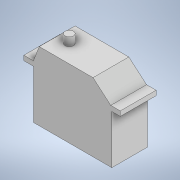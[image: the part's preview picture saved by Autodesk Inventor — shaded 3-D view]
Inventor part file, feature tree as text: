
AUTODESK INVENTOR PART (.ipt)
format: ipt  version: 2020 (Build 240168000, 168)  size: 116,224 bytes
history: native  units: mm
features: extrude x2, sketch x2
ambient origin geometry x8: Origin, YZ Plane, XZ Plane, XY Plane, X Axis, Y Axis, Z Axis, Center Point
bodies: Solid1 (feature_tree)
feature tree (4):
  extrude  "Extrusion1"  Depth=40.8mm
  extrude  "Extrusion2"  Depth=30.0mm TaperAngle=0.0deg
  sketch  "Sketch1"  dims[d0=65.7mm d1=40.8mm]
  sketch  "Sketch2"  dims[d2=4.0mm d3=30.0mm d4=0.0mm d5=7.0mm d6=15.0mm d7=15.0mm d9=57.5mm d10=7.0mm d11=0.0mm d13=8.0mm d14=8.0mm]
